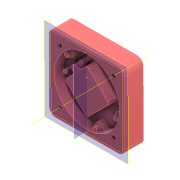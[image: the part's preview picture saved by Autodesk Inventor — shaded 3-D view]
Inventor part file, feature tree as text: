
AUTODESK INVENTOR PART (.ipt)
format: ipt  version: 2022 (Build 260153000, 153)  size: 447,488 bytes
history: native  units: mm
features: sketch x6, other x5, plane x4, extrude x2, fillet x2, projected_geometry x2, hole x1, imported_body x1, revolve x1, pattern_circular x1, reference x1
ambient origin geometry x8: Origin, YZ Plane, XZ Plane, XY Plane, X Axis, Y Axis, Z Axis, Center Point
bodies: Volumenkörper1 (feature_tree), Volumenkörper3 (feature_tree), Volumenkörper4 (feature_tree), Volumenkörper5 (feature_tree)
feature tree (26):
  plane  "Arbeitsebene1"
  extrude  "Extrusion1"  Depth=60.0mm
  fillet  "Rundung1"  Radius=5.0mm
  hole  "Bohrung1"  [1 undecoded]
  imported_body  "Basis2"
  other  "Kombinieren1"
  plane  "Arbeitsebene2"
  other  "Trennen1"
  extrude  "Extrusion3"  Depth=10.0mm
  plane  "Arbeitsebene3"
  plane  "Arbeitsebene4"
  revolve  "Umdrehung1"
  pattern_circular  "Runde Anordnung2"  [2 undecoded]
  fillet  "Rundung7"  Radius=12.5mm
  sketch  "Skizze8"  dims[d20=0.0mm d21=0.349066mm d23=-30.0mm d32=12.5mm d34=2.0mm d35=0.8mm d36=360.0deg d38=40.0mm d39=360.0deg d41=0.5mm d42=0.0mm]
  sketch  "Skizze1"  dims[d0=60.0mm d1=60.0mm]
  reference  "Referenz1"
  sketch  "Skizze2"  dims[d2=10.0mm d3=15.0mm d4=0.0mm d5=0.0mm d6=5.0mm]
  projected_geometry  "Projizierte Kontur1"
  sketch  "Skizze4"  dims[d7=60.0mm]
  sketch  "Skizze5"  dims[d8=3.2mm d9=6.0mm d10=6.5mm d11=4.0mm d12=90.0deg d13=8.0mm d14=20.594885mm d17=-15.5mm]
  sketch  "Skizze7"  dims[d18=10.0mm d19=4.0mm]
  projected_geometry  "Projizierte Kontur2"
  other  "IM_Mold_plate_top.ipt.iam"
  other  "IM_Matchboxscope_plate:1"
  other  "Baugruppe1"
note: 3 required parameter values undecoded (feature->parameter linkage not recoverable at this tier; creation-order binding heuristic only, values carry confidence <= 0.55)
